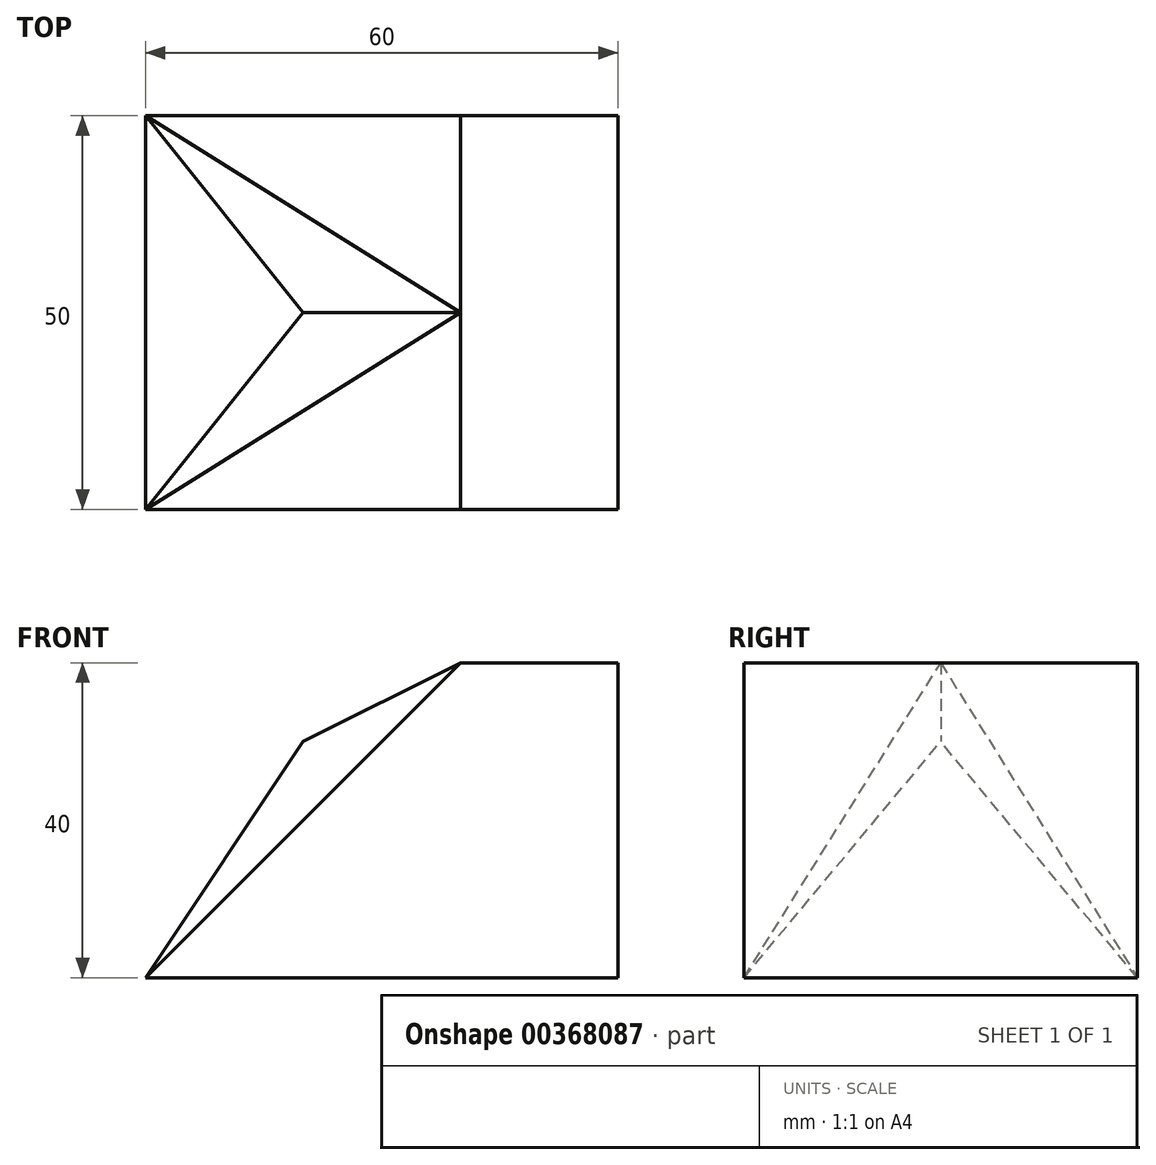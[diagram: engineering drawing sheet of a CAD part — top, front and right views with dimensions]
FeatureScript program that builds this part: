
annotation { "Feature Type Name" : "Feature", "Feature Type Description" : "" }
export const myFeature = defineFeature(function(context is Context, id is Id, definition is map)
    precondition{}
    {
        {
            var Q0;
            Q0=qCreatedBy(makeId("Front.planeOp"),FACE);
            var sketch = newSketch(context, id + "F0", { "sketchPlane" : qUnion([Q0])});
            skLineSegment(sketch, "E0", {"start": v(0, 0) * mm, "end": v(0, 40) * mm});
            skLineSegment(sketch, "E1", {"start": v(0, 40) * mm, "end": v(-20, 40) * mm});
            skLineSegment(sketch, "E2", {"start": v(-20, 40) * mm, "end": v(-60, 0) * mm});
            skLineSegment(sketch, "E3", {"start": v(-60, 0) * mm, "end": v(0, 0) * mm});
            skPoint(sketch, "E4", {"position": v(-40, 30) * mm});
            skSolve(sketch);
        }
        {
            var Q0;
            Q0=makeQuery(id+"F0.imprint","IMPRINT",FACE,{"disambiguationData":[TD([[makeQuery(id+"F0.imprint","IMPRINT",EDGE,{"derivedFrom":sQuery(id+"F0.wireOp",EDGE,"E0")}),1.0]])]});
            extrude(context, id + "F1", {"entities" : qUnion([Q0]), "depth" : 25 * mm, "hasSecondDirection" : true, "secondDirectionOppositeDirection" : true, "secondDirectionDepth" : 25 * mm});
        }
        {
            var Q0;
            Q0=makeQuery(id+"F1.opExtrude","SWEPT_FACE",FACE,{"disambiguationData":[OSD([sQuery(id+"F0.wireOp",EDGE,"E2")])]});
            var sketch = newSketch(context, id + "F2", { "sketchPlane" : qUnion([Q0])});
            skLineSegment(sketch, "E5", {"start": v(0, 14.14) * mm, "end": v(-25, -42.43) * mm});
            skLineSegment(sketch, "E6", {"start": v(25, -42.43) * mm, "end": v(0, 14.14) * mm});
            skSolve(sketch);
        }
        {
            var Q1;
            Q1=makeQuery(id+"F2.imprint","IMPRINT",FACE,{"disambiguationData":[TD([[makeQuery(id+"F2.imprint","IMPRINT",EDGE,{"derivedFrom":sQuery(id+"F2.wireOp",EDGE,"E5")}),1.0]])]});
            var Q2;
            Q2=sQuery(id+"F0.wireOp",VERTEX,"E4");
            loft(context, id + "F3", {"operationType" : NewBodyOperationType.ADD, "sheetProfilesArray" : [{ "sheetProfileEntities" : qUnion([Q1]) }, { "sheetProfileEntities" : qUnion([Q2]) }]});
        }
    });
